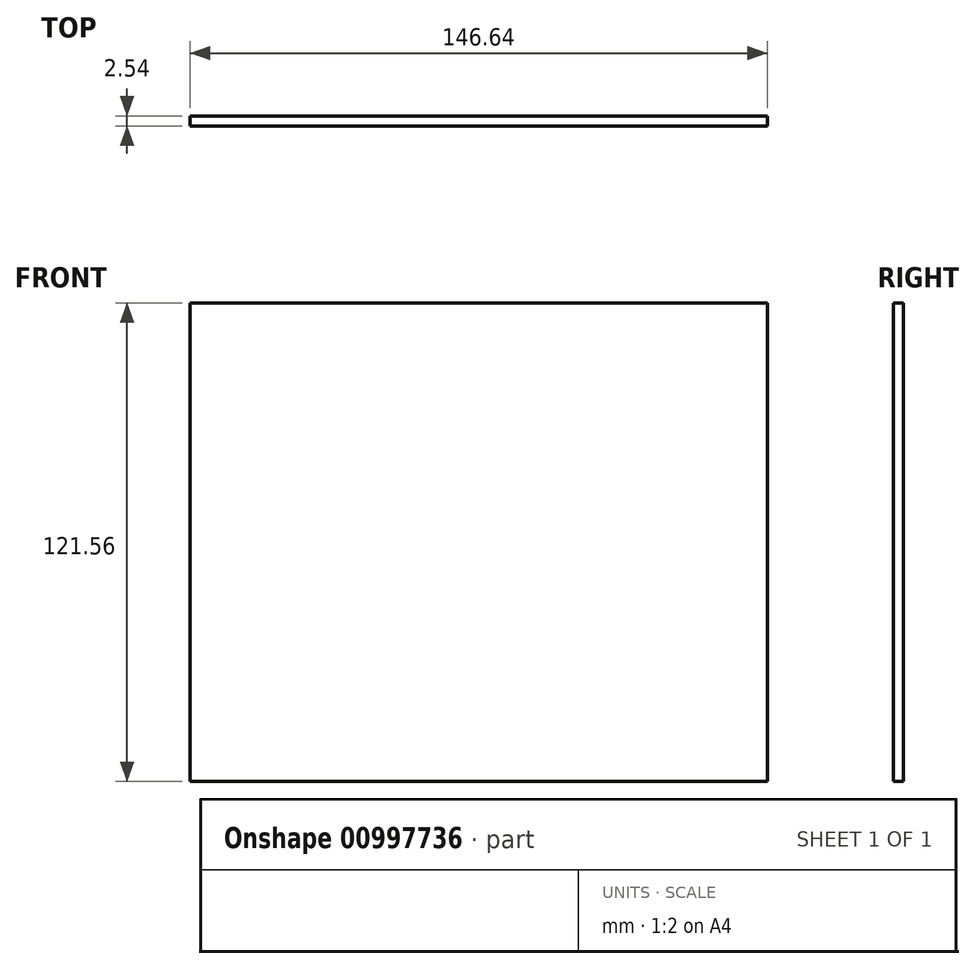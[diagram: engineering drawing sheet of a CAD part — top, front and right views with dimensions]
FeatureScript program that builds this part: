
annotation { "Feature Type Name" : "Feature", "Feature Type Description" : "" }
export const myFeature = defineFeature(function(context is Context, id is Id, definition is map)
    precondition{}
    {
        {
            var Q0;
            Q0=qCreatedBy(makeId("Front.planeOp"),FACE);
            var sketch = newSketch(context, id + "F0", { "sketchPlane" : qUnion([Q0])});
            skLineSegment(sketch, "E0.bottom", {"start": v(-74.29, 58.61) * mm, "end": v(72.35, 58.61) * mm});
            skLineSegment(sketch, "E0.top", {"start": v(-74.29, -62.95) * mm, "end": v(72.35, -62.95) * mm});
            skLineSegment(sketch, "E0.left", {"start": v(-74.29, 58.61) * mm, "end": v(-74.29, -62.95) * mm});
            skLineSegment(sketch, "E0.right", {"start": v(72.35, 58.61) * mm, "end": v(72.35, -62.95) * mm});
            skSolve(sketch);
        }
        {
            var Q0;
            Q0=makeQuery(id+"F0.imprint","IMPRINT",FACE,{"disambiguationData":[TD([[makeQuery(id+"F0.imprint","IMPRINT",EDGE,{"derivedFrom":sQuery(id+"F0.wireOp",EDGE,"E0.bottom")}),-1.0]])]});
            extrude(context, id + "F1", {"entities" : qUnion([Q0]), "depth" : 2.54 * mm, "offsetDistance" : 25.4 * mm});
        }
    });
